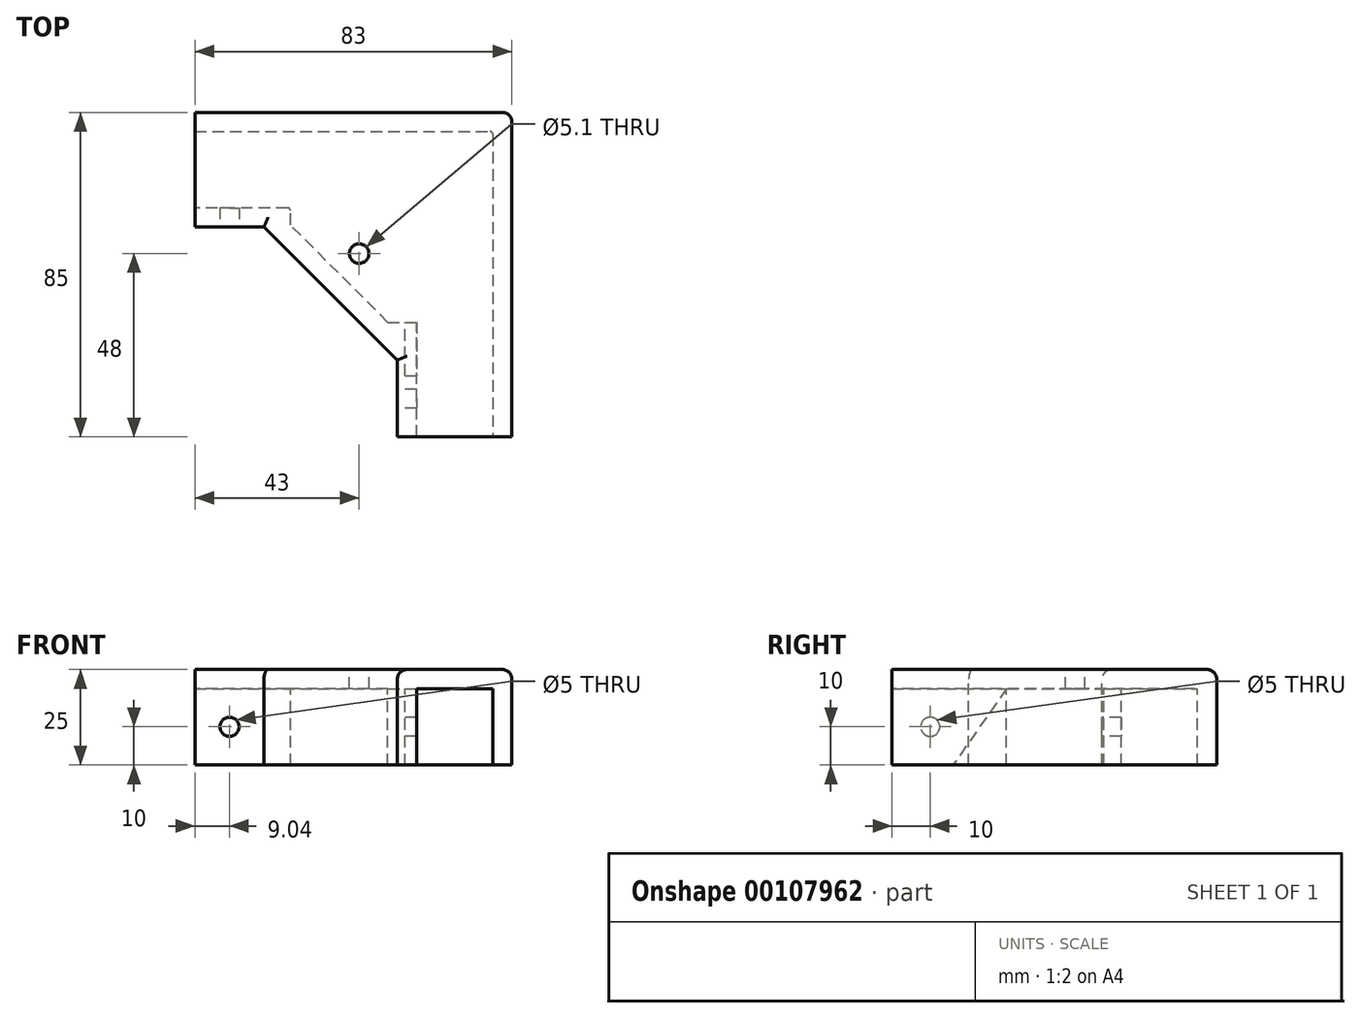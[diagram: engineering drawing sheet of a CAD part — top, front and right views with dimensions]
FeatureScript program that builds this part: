
annotation { "Feature Type Name" : "Feature", "Feature Type Description" : "" }
export const myFeature = defineFeature(function(context is Context, id is Id, definition is map)
    precondition{}
    {
        {
            var Q0;
            Q0=qCreatedBy(makeId("Top.planeOp"),FACE);
            var sketch = newSketch(context, id + "F0", { "sketchPlane" : qUnion([Q0])});
            skLineSegment(sketch, "E0", {"start": v(-83, 0) * mm, "end": v(0, 0) * mm});
            skLineSegment(sketch, "E1", {"start": v(0, 0) * mm, "end": v(0, -85) * mm});
            skLineSegment(sketch, "E2", {"start": v(0, -85) * mm, "end": v(-30, -85) * mm});
            skLineSegment(sketch, "E3", {"start": v(-64.92, -30) * mm, "end": v(-83, -30) * mm});
            skLineSegment(sketch, "E4", {"start": v(-83, -30) * mm, "end": v(-83, 0) * mm});
            skLineSegment(sketch, "E5", {"start": v(-57.88, -5) * mm, "end": v(43.34, -5) * mm, "construction": true});
            skLineSegment(sketch, "E6", {"start": v(-5, 29.8) * mm, "end": v(-5, -87.13) * mm, "construction": true});
            skLineSegment(sketch, "E7", {"start": v(-57.88, -25) * mm, "end": v(100.82, -25) * mm, "construction": true});
            skLineSegment(sketch, "E8", {"start": v(-25, 29.8) * mm, "end": v(-25, -93.74) * mm, "construction": true});
            skLineSegment(sketch, "E9", {"start": v(-58, -25) * mm, "end": v(-58, -29.5) * mm, "construction": true});
            skLineSegment(sketch, "E10", {"start": v(-58, -29.5) * mm, "end": v(-32.5, -55) * mm, "construction": true});
            skLineSegment(sketch, "E11", {"start": v(-32.5, -55) * mm, "end": v(-25, -55) * mm, "construction": true});
            skCircle(sketch, "E12", {"center": v(-40, -37) * mm, "radius": 2.55 * mm});
            skLineSegment(sketch, "E13", {"start": v(-30, -64.92) * mm, "end": v(-64.92, -30) * mm});
            skLineSegment(sketch, "E14", {"start": v(-30, -64.92) * mm, "end": v(-30, -85) * mm});
            skLineSegment(sketch, "E15", {"start": v(-57.88, -5) * mm, "end": v(-124.41, -5) * mm, "construction": true});
            skLineSegment(sketch, "E16", {"start": v(-57.88, -25) * mm, "end": v(-124.41, -25) * mm, "construction": true});
            skLineSegment(sketch, "E17", {"start": v(-83, -5) * mm, "end": v(-5, -5) * mm});
            skLineSegment(sketch, "E18", {"start": v(-5, -5) * mm, "end": v(-5, -85) * mm});
            skLineSegment(sketch, "E19", {"start": v(-5, -85) * mm, "end": v(-25, -85) * mm});
            skLineSegment(sketch, "E20", {"start": v(-25, -85) * mm, "end": v(-25, -55) * mm});
            skLineSegment(sketch, "E21", {"start": v(-32.5, -55) * mm, "end": v(-58, -29.5) * mm});
            skLineSegment(sketch, "E22", {"start": v(-57.88, -25) * mm, "end": v(-83, -25) * mm});
            skLineSegment(sketch, "E23", {"start": v(-83, -25) * mm, "end": v(-83, -5) * mm});
            skLineSegment(sketch, "E24", {"start": v(-32.5, -55) * mm, "end": v(-25, -55) * mm});
            skLineSegment(sketch, "E25", {"start": v(-58, -29.5) * mm, "end": v(-58, -25) * mm});
            skSolve(sketch);
        }
        {
            var Q0;
            {var subQ1=sQuery(id+"F0.wireOp",EDGE,"E3");Q0=makeQuery(id+"F0.imprint","IMPRINT",FACE,{"disambiguationData":[TD([[makeQuery(id+"F0.imprint","IMPRINT",EDGE,{"derivedFrom":subQ1}),-1.0]])]});}
            var Q1;
            {var subQ1=sQuery(id+"F0.wireOp",EDGE,"E0");Q1=makeQuery(id+"F0.imprint","IMPRINT",FACE,{"disambiguationData":[TD([[makeQuery(id+"F0.imprint","IMPRINT",EDGE,{"derivedFrom":subQ1}),-1.0]])]});}
            var Q2;
            Q2=makeQuery(id+"F0.imprint","IMPRINT",FACE,{"disambiguationData":[TD([[makeQuery(id+"F0.imprint","IMPRINT",EDGE,{"derivedFrom":sQuery(id+"F0.wireOp",EDGE,"E12")}),-1.0]])]});
            extrude(context, id + "F1", {"entities" : qUnion([Q0, Q1, Q2]), "oppositeDirection" : true, "depth" : 5 * mm});
        }
        {
            var Q0;
            {var subQ1=sQuery(id+"F0.wireOp",EDGE,"E3");Q0=makeQuery(id+"F0.imprint","IMPRINT",FACE,{"disambiguationData":[TD([[makeQuery(id+"F0.imprint","IMPRINT",EDGE,{"derivedFrom":subQ1}),-1.0]])]});}
            var Q1;
            {var subQ1=sQuery(id+"F0.wireOp",EDGE,"E0");Q1=makeQuery(id+"F0.imprint","IMPRINT",FACE,{"disambiguationData":[TD([[makeQuery(id+"F0.imprint","IMPRINT",EDGE,{"derivedFrom":subQ1}),-1.0]])]});}
            extrude(context, id + "F2", {"entities" : qUnion([Q0, Q1]), "operationType" : NewBodyOperationType.ADD, "oppositeDirection" : true, "depth" : 25 * mm});
        }
        {
            var Q0;
            Q0=makeQuery(id+"F1.opExtrude","CAP_EDGE",EDGE,{"disambiguationData":[OSD([sQuery(id+"F0.wireOp",EDGE,"E3")])],"isStart":true});
            var Q1;
            Q1=makeQuery(id+"F1.opExtrude","CAP_EDGE",EDGE,{"disambiguationData":[OSD([sQuery(id+"F0.wireOp",EDGE,"E13")])],"isStart":true});
            var Q2;
            Q2=makeQuery(id+"F1.opExtrude","CAP_EDGE",EDGE,{"disambiguationData":[OSD([sQuery(id+"F0.wireOp",EDGE,"E14")])],"isStart":true});
            var Q3;
            Q3=makeQuery(id+"F1.opExtrude","CAP_EDGE",EDGE,{"disambiguationData":[OSD([sQuery(id+"F0.wireOp",EDGE,"E1")])],"isStart":true});
            var Q4;
            Q4=makeQuery(id+"F1.opExtrude","CAP_EDGE",EDGE,{"disambiguationData":[OSD([sQuery(id+"F0.wireOp",EDGE,"E0")])],"isStart":true});
            var Q5;
            {var subQ0=sQuery(id+"F0.wireOp",EDGE,"E1");var subQ1=sQuery(id+"F0.wireOp",EDGE,"E0");Q5=makeQuery(id+"F2.boolean.opBoolean","MERGE",EDGE,{"derivedFrom":[makeQuery(id+"F1.opExtrude","SWEPT_EDGE",EDGE,{"disambiguationData":[OSD([subQ1,subQ0])]}),makeQuery(id+"F2.opExtrude","SWEPT_EDGE",EDGE,{"disambiguationData":[OSD([subQ1,subQ0])]})]});}
            fillet(context, id + "F3", {"entities" : qUnion([Q0, Q1, Q2, Q3, Q4, Q5]), "radius" : 2.5 * mm, "tangentPropagation" : true, "allowEdgeOverflow" : false});
        }
        {
            var Q0;
            Q0=makeQuery(id+"F2.opExtrude","SWEPT_FACE",FACE,{"disambiguationData":[OSD([sQuery(id+"F0.wireOp",EDGE,"E20")])]});
            var sketch = newSketch(context, id + "F4", { "sketchPlane" : qUnion([Q0])});
            skLineSegment(sketch, "E26", {"start": v(-55, -5) * mm, "end": v(-69, -25) * mm});
            skLineSegment(sketch, "E27", {"start": v(-69, -25) * mm, "end": v(-55, -25) * mm});
            skLineSegment(sketch, "E28", {"start": v(-55, -25) * mm, "end": v(-55, -5) * mm});
            skSolve(sketch);
        }
        {
            var Q0;
            Q0=makeQuery(id+"F4.imprint","IMPRINT",FACE,{"disambiguationData":[TD([[makeQuery(id+"F4.imprint","IMPRINT",EDGE,{"derivedFrom":sQuery(id+"F4.wireOp",EDGE,"E26")}),1.0]])]});
            extrude(context, id + "F5", {"entities" : qUnion([Q0]), "operationType" : NewBodyOperationType.REMOVE, "oppositeDirection" : true, "depth" : 3 * mm});
        }
        {
            var Q0;
            Q0=makeQuery(id+"F2.opExtrude","SWEPT_EDGE",EDGE,{"disambiguationData":[OSD([sQuery(id+"F0.wireOp",EDGE,"E22"),sQuery(id+"F0.wireOp",EDGE,"E25")])]});
            var Q1;
            Q1=makeQuery(id+"F5.boolean.opBoolean","COPY",EDGE,{"derivedFrom":makeQuery(id+"F5.opExtrude","CAP_EDGE",EDGE,{"disambiguationData":[OSD([sQuery(id+"F4.wireOp",EDGE,"E28")])],"isStart":false})});
            var Q2;
            Q2=makeQuery(id+"F5.boolean.opBoolean","COPY",EDGE,{"derivedFrom":makeQuery(id+"F5.opExtrude","CAP_EDGE",EDGE,{"disambiguationData":[OSD([sQuery(id+"F4.wireOp",EDGE,"E26")])],"isStart":true})});
            var Q3;
            Q3=makeQuery(id+"F2.opExtrude","SWEPT_EDGE",EDGE,{"disambiguationData":[OSD([sQuery(id+"F0.wireOp",EDGE,"E17"),sQuery(id+"F0.wireOp",EDGE,"E18")])]});
            fillet(context, id + "F6", {"entities" : qUnion([Q0, Q1, Q2, Q3]), "radius" : .75 * mm, "tangentPropagation" : true, "allowEdgeOverflow" : false});
        }
        {
            var Q0;
            {var subQ0=sQuery(id+"F0.wireOp",EDGE,"E14");Q0=makeQuery(id+"F2.boolean.opBoolean","MERGE",FACE,{"derivedFrom":[makeQuery(id+"F1.opExtrude","SWEPT_FACE",FACE,{"disambiguationData":[OSD([subQ0])]}),makeQuery(id+"F2.opExtrude","SWEPT_FACE",FACE,{"disambiguationData":[OSD([subQ0])]})]});}
            var sketch = newSketch(context, id + "F7", { "sketchPlane" : qUnion([Q0])});
            skPoint(sketch, "E29", {"position": v(75, -15) * mm});
            skSolve(sketch);
        }
        {
            var Q0;
            Q0=sQuery(id+"F7.wireOp",VERTEX,"E29");
            var Q1;
            Q1=makeQuery(id+"F1.opExtrude","SWEPT_BODY",BODY,{"disambiguationData":[OSD([sQuery(id+"F0.wireOp",EDGE,"E0"),sQuery(id+"F0.wireOp",EDGE,"E1"),sQuery(id+"F0.wireOp",EDGE,"E2"),sQuery(id+"F0.wireOp",EDGE,"E3"),sQuery(id+"F0.wireOp",EDGE,"E4"),sQuery(id+"F0.wireOp",EDGE,"E12"),sQuery(id+"F0.wireOp",EDGE,"E13"),sQuery(id+"F0.wireOp",EDGE,"E14"),sQuery(id+"F0.wireOp",EDGE,"E19"),sQuery(id+"F0.wireOp",EDGE,"E23")])]});
            hole(context, id + "F8", {"style" : HoleStyle.SIMPLE, "endStyle" : HoleEndStyle.BLIND, "holeDiameter" : 5 * mm, "holeDepth" : 6 * mm, "locations" : qUnion([Q0]), "scope" : qUnion([Q1])});
        }
        {
            var Q0;
            {var subQ0=sQuery(id+"F0.wireOp",EDGE,"E3");Q0=makeQuery(id+"F2.boolean.opBoolean","MERGE",FACE,{"derivedFrom":[makeQuery(id+"F1.opExtrude","SWEPT_FACE",FACE,{"disambiguationData":[OSD([subQ0])]}),makeQuery(id+"F2.opExtrude","SWEPT_FACE",FACE,{"disambiguationData":[OSD([subQ0])]})]});}
            var sketch = newSketch(context, id + "F9", { "sketchPlane" : qUnion([Q0])});
            skLineSegment(sketch, "E30", {"start": v(-73.96, -25) * mm, "end": v(-73.96, -2.5) * mm, "construction": true});
            skPoint(sketch, "E31", {"position": v(-73.96, -15) * mm});
            skSolve(sketch);
        }
        {
            var Q0;
            Q0=sQuery(id+"F9.wireOp",VERTEX,"E31");
            var Q1;
            Q1=makeQuery(id+"F1.opExtrude","SWEPT_BODY",BODY,{"disambiguationData":[OSD([sQuery(id+"F0.wireOp",EDGE,"E0"),sQuery(id+"F0.wireOp",EDGE,"E1"),sQuery(id+"F0.wireOp",EDGE,"E2"),sQuery(id+"F0.wireOp",EDGE,"E3"),sQuery(id+"F0.wireOp",EDGE,"E4"),sQuery(id+"F0.wireOp",EDGE,"E12"),sQuery(id+"F0.wireOp",EDGE,"E13"),sQuery(id+"F0.wireOp",EDGE,"E14"),sQuery(id+"F0.wireOp",EDGE,"E19"),sQuery(id+"F0.wireOp",EDGE,"E23")])]});
            hole(context, id + "F10", {"style" : HoleStyle.SIMPLE, "endStyle" : HoleEndStyle.BLIND, "holeDiameter" : 5 * mm, "holeDepth" : 6 * mm, "locations" : qUnion([Q0]), "scope" : qUnion([Q1])});
        }
    });
